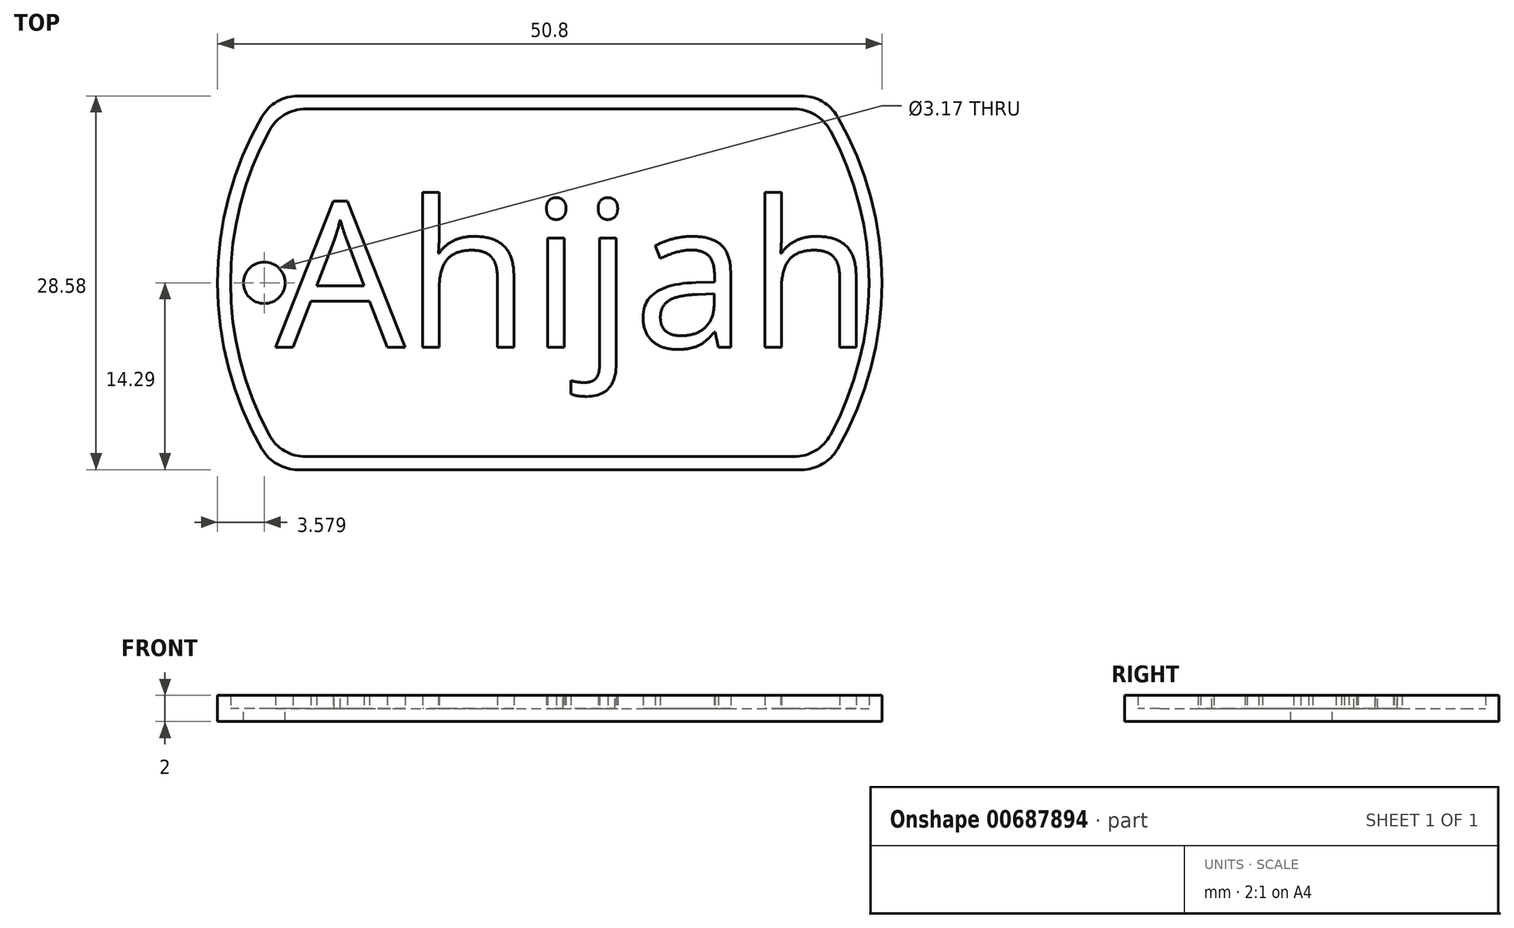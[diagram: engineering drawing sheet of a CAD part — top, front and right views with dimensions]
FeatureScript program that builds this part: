
annotation { "Feature Type Name" : "Feature", "Feature Type Description" : "" }
export const myFeature = defineFeature(function(context is Context, id is Id, definition is map)
    precondition{}
    {
        {
            var Q0;
            Q0=qCreatedBy(makeId("Top.planeOp"),FACE);
            var sketch = newSketch(context, id + "F0", { "sketchPlane" : qUnion([Q0])});
            skArc(sketch, "E0", {"start": v(-22, 12.7) * mm, "mid": v(-25.4, 0) * mm, "end": v(-22, -12.7) * mm});
            skLineSegment(sketch, "E1.top", {"start": v(-19.25, -14.29) * mm, "end": v(19.25, -14.29) * mm});
            skArc(sketch, "E2.trimOffspring", {"start": v(22, -12.7) * mm, "mid": v(25.4, 0) * mm, "end": v(22, 12.7) * mm});
            skLineSegment(sketch, "E3", {"start": v(-19.25, 14.29) * mm, "end": v(19.25, 14.29) * mm});
            skPoint(sketch, "E4.visualSharp", {"position": v(-21, 14.29) * mm});
            skArc(sketch, "E4.filletArc", {"start": v(-19.25, 14.29) * mm, "mid": v(-20.83, 13.86) * mm, "end": v(-22, 12.7) * mm});
            skPoint(sketch, "E5.visualSharp", {"position": v(21, 14.29) * mm});
            skArc(sketch, "E5.filletArc", {"start": v(22, 12.7) * mm, "mid": v(20.83, 13.86) * mm, "end": v(19.25, 14.29) * mm});
            skPoint(sketch, "E6.visualSharp", {"position": v(21, -14.29) * mm});
            skArc(sketch, "E6.filletArc", {"start": v(19.25, -14.29) * mm, "mid": v(20.83, -13.86) * mm, "end": v(22, -12.7) * mm});
            skPoint(sketch, "E7.visualSharp", {"position": v(-21, -14.29) * mm});
            skArc(sketch, "E7.filletArc", {"start": v(-22, -12.7) * mm, "mid": v(-20.83, -13.86) * mm, "end": v(-19.25, -14.29) * mm});
            skSolve(sketch);
        }
        {
            var Q0;
            Q0=makeQuery(id+"F0.imprint","IMPRINT",FACE,{"disambiguationData":[TD([[makeQuery(id+"F0.imprint","IMPRINT",EDGE,{"derivedFrom":sQuery(id+"F0.wireOp",EDGE,"E0")}),1.0]])]});
            extrude(context, id + "F1", {"entities" : qUnion([Q0]), "depth" : 1 * mm, "offsetDistance" : 25.4 * mm});
        }
        {
            var Q0;
            Q0=makeQuery(id+"F1.opExtrude","CAP_FACE",FACE,{"disambiguationData":[OSD([sQuery(id+"F0.wireOp",EDGE,"E0"),sQuery(id+"F0.wireOp",EDGE,"E1.top"),sQuery(id+"F0.wireOp",EDGE,"E2.trimOffspring"),sQuery(id+"F0.wireOp",EDGE,"E3"),sQuery(id+"F0.wireOp",EDGE,"E4.filletArc"),sQuery(id+"F0.wireOp",EDGE,"E5.filletArc"),sQuery(id+"F0.wireOp",EDGE,"E6.filletArc"),sQuery(id+"F0.wireOp",EDGE,"E7.filletArc")])],"isStart":false});
            var sketch = newSketch(context, id + "F2", { "sketchPlane" : qUnion([Q0])});
            skLineSegment(sketch, "E8.0", {"start": v(-18.66, 13.29) * mm, "end": v(18.66, 13.29) * mm});
            skArc(sketch, "E8.1", {"start": v(-21.45, 11.63) * mm, "mid": v(-24.4, 0) * mm, "end": v(-21.45, -11.63) * mm});
            skLineSegment(sketch, "E8.2", {"start": v(-18.66, -13.29) * mm, "end": v(18.66, -13.29) * mm});
            skArc(sketch, "E8.3", {"start": v(21.45, -11.63) * mm, "mid": v(24.4, 0) * mm, "end": v(21.45, 11.63) * mm});
            skPoint(sketch, "E9.visualSharp", {"position": v(-20.46, 13.29) * mm});
            skArc(sketch, "E9.filletArc", {"start": v(-18.66, 13.29) * mm, "mid": v(-20.29, 12.84) * mm, "end": v(-21.45, 11.63) * mm});
            skPoint(sketch, "E10.visualSharp", {"position": v(20.46, 13.29) * mm});
            skArc(sketch, "E10.filletArc", {"start": v(21.45, 11.63) * mm, "mid": v(20.29, 12.84) * mm, "end": v(18.66, 13.29) * mm});
            skPoint(sketch, "E11.visualSharp", {"position": v(20.46, -13.29) * mm});
            skArc(sketch, "E11.filletArc", {"start": v(18.66, -13.29) * mm, "mid": v(20.29, -12.84) * mm, "end": v(21.45, -11.63) * mm});
            skPoint(sketch, "E12.visualSharp", {"position": v(-20.46, -13.29) * mm});
            skArc(sketch, "E12.filletArc", {"start": v(-21.45, -11.63) * mm, "mid": v(-20.29, -12.84) * mm, "end": v(-18.66, -13.29) * mm});
            skLineSegment(sketch, "E13.0", {"start": v(-19.25, 14.29) * mm, "end": v(19.25, 14.29) * mm});
            skArc(sketch, "E13.1", {"start": v(-22, 12.7) * mm, "mid": v(-25.4, 0) * mm, "end": v(-22, -12.7) * mm});
            skLineSegment(sketch, "E13.2", {"start": v(-19.25, -14.29) * mm, "end": v(19.25, -14.29) * mm});
            skArc(sketch, "E13.3", {"start": v(22, -12.7) * mm, "mid": v(25.4, 0) * mm, "end": v(22, 12.7) * mm});
            skPoint(sketch, "E14.visualSharp", {"position": v(-21, -14.29) * mm});
            skArc(sketch, "E14.filletArc", {"start": v(-22, -12.7) * mm, "mid": v(-20.83, -13.86) * mm, "end": v(-19.25, -14.29) * mm});
            skPoint(sketch, "E15.visualSharp", {"position": v(21, -14.29) * mm});
            skArc(sketch, "E15.filletArc", {"start": v(19.25, -14.29) * mm, "mid": v(20.83, -13.86) * mm, "end": v(22, -12.7) * mm});
            skPoint(sketch, "E16.visualSharp", {"position": v(21, 14.29) * mm});
            skArc(sketch, "E16.filletArc", {"start": v(22, 12.7) * mm, "mid": v(20.83, 13.86) * mm, "end": v(19.25, 14.29) * mm});
            skPoint(sketch, "E17.visualSharp", {"position": v(-21, 14.29) * mm});
            skArc(sketch, "E17.filletArc", {"start": v(-19.25, 14.29) * mm, "mid": v(-20.83, 13.86) * mm, "end": v(-22, 12.7) * mm});
            skSolve(sketch);
        }
        {
            var Q0;
            Q0=makeQuery(id+"F2.imprint","IMPRINT",FACE,{"disambiguationData":[TD([[makeQuery(id+"F2.imprint","IMPRINT",EDGE,{"derivedFrom":sQuery(id+"F2.wireOp",EDGE,"E8.0")}),1.0]])]});
            extrude(context, id + "F3", {"entities" : qUnion([Q0]), "operationType" : NewBodyOperationType.ADD, "depth" : 1 * mm, "offsetDistance" : 25.4 * mm});
        }
        {
            var Q0;
            Q0=makeQuery(id+"F1.opExtrude","CAP_FACE",FACE,{"disambiguationData":[OSD([sQuery(id+"F0.wireOp",EDGE,"E0"),sQuery(id+"F0.wireOp",EDGE,"E1.top"),sQuery(id+"F0.wireOp",EDGE,"E2.trimOffspring"),sQuery(id+"F0.wireOp",EDGE,"E3"),sQuery(id+"F0.wireOp",EDGE,"E4.filletArc"),sQuery(id+"F0.wireOp",EDGE,"E5.filletArc"),sQuery(id+"F0.wireOp",EDGE,"E6.filletArc"),sQuery(id+"F0.wireOp",EDGE,"E7.filletArc")])],"isStart":false});
            var sketch = newSketch(context, id + "F4", { "sketchPlane" : qUnion([Q0])});
            skCircle(sketch, "E18", {"center": v(-21.82, 0) * mm, "radius": 1.59 * mm});
            skSolve(sketch);
        }
        {
            var Q0;
            Q0=makeQuery(id+"F4.imprint","IMPRINT",FACE,{"disambiguationData":[TD([[makeQuery(id+"F4.imprint","IMPRINT",EDGE,{"derivedFrom":sQuery(id+"F4.wireOp",EDGE,"E18")}),1.0]])]});
            extrude(context, id + "F5", {"entities" : qUnion([Q0]), "operationType" : NewBodyOperationType.REMOVE, "oppositeDirection" : true, "depth" : 1 * mm, "offsetDistance" : 25.4 * mm});
        }
        {
            var Q0;
            Q0=makeQuery(id+"F2.imprint","IMPRINT",FACE,{"disambiguationData":[TD([[makeQuery(id+"F2.imprint","IMPRINT",EDGE,{"derivedFrom":sQuery(id+"F2.wireOp",EDGE,"E8.0")}),-1.0]])]});
            var sketch = newSketch(context, id + "F6", { "sketchPlane" : qUnion([Q0])});
            skText(sketch, "E19", { "text": "Ahijah", "fontName": "OpenSans-Regular.ttf"});
            const initialGuessF6  = {"E19": [-0.02095, -0.00494, 1, 0, 0.01124]};
            skSetInitialGuess(sketch, initialGuessF6);
            skSolve(sketch);
        }
        {
            var Q0;
            Q0 = qSketchRegion(id + "F6", true);
            extrude(context, id + "F7", {"entities" : qUnion([Q0]), "operationType" : NewBodyOperationType.ADD, "depth" : 1 * mm, "offsetDistance" : 25.4 * mm});
        }
    });
